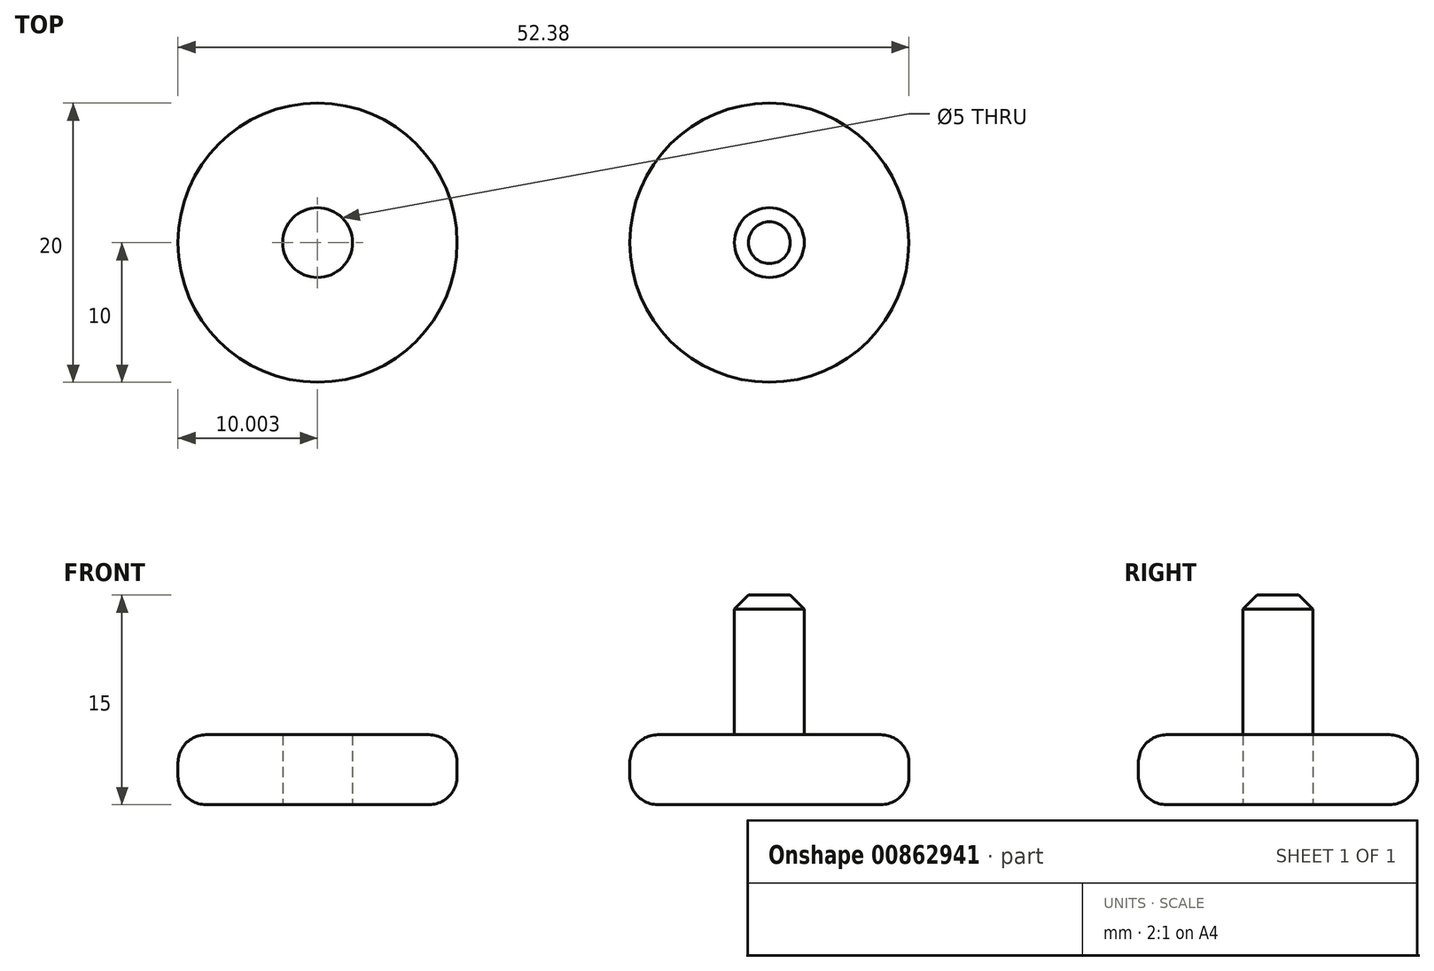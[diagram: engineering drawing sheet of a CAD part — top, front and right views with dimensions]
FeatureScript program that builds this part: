
annotation { "Feature Type Name" : "Feature", "Feature Type Description" : "" }
export const myFeature = defineFeature(function(context is Context, id is Id, definition is map)
    precondition{}
    {
        {
            var Q0;
            Q0=qCreatedBy(makeId("Top.planeOp"),FACE);
            var sketch = newSketch(context, id + "F0", { "sketchPlane" : qUnion([Q0])});
            skCircle(sketch, "E0", {"center": v(0, 0) * mm, "radius": 10 * mm});
            skCircle(sketch, "E1", {"center": v(-32.38, 0) * mm, "radius": 10 * mm});
            skCircle(sketch, "E2", {"center": v(-32.38, 0) * mm, "radius": 2.5 * mm});
            skSolve(sketch);
        }
        {
            var Q0;
            Q0=makeQuery(id+"F0.imprint","IMPRINT",FACE,{"disambiguationData":[TD([[makeQuery(id+"F0.imprint","IMPRINT",EDGE,{"derivedFrom":sQuery(id+"F0.wireOp",EDGE,"E0")}),1.0]])]});
            extrude(context, id + "F1", {"entities" : qUnion([Q0]), "depth" : 5 * mm, "offsetDistance" : 25 * mm});
        }
        {
            var Q0;
            Q0=makeQuery(id+"F1.opExtrude","CAP_FACE",FACE,{"disambiguationData":[OSD([sQuery(id+"F0.wireOp",EDGE,"E0")])],"isStart":false});
            var sketch = newSketch(context, id + "F2", { "sketchPlane" : qUnion([Q0])});
            skCircle(sketch, "E3", {"center": v(0, 0) * mm, "radius": 2.5 * mm});
            skSolve(sketch);
        }
        {
            var Q0;
            Q0=makeQuery(id+"F2.imprint","IMPRINT",FACE,{"disambiguationData":[TD([[makeQuery(id+"F2.imprint","IMPRINT",EDGE,{"derivedFrom":sQuery(id+"F2.wireOp",EDGE,"E3")}),1.0]])]});
            extrude(context, id + "F3", {"entities" : qUnion([Q0]), "operationType" : NewBodyOperationType.ADD, "depth" : 10 * mm, "offsetDistance" : 25 * mm});
        }
        {
            var Q0;
            Q0=makeQuery(id+"F3.opExtrude","CAP_EDGE",EDGE,{"disambiguationData":[OSD([sQuery(id+"F2.wireOp",EDGE,"E3")])],"isStart":false});
            chamfer(context, id + "F4", {"entities" : qUnion([Q0]), "width" : 1 * mm, "tangentPropagation" : true});
        }
        {
            var Q0;
            Q0=makeQuery(id+"F1.opExtrude","CAP_EDGE",EDGE,{"disambiguationData":[OSD([sQuery(id+"F0.wireOp",EDGE,"E0")])],"isStart":false});
            var Q1;
            Q1=makeQuery(id+"F1.opExtrude","CAP_EDGE",EDGE,{"disambiguationData":[OSD([sQuery(id+"F0.wireOp",EDGE,"E0")])],"isStart":true});
            fillet(context, id + "F5", {"entities" : qUnion([Q0, Q1]), "radius" : 2 * mm, "tangentPropagation" : true, "allowEdgeOverflow" : false});
        }
        {
            var Q0;
            Q0 = qSketchRegion(id + "F0", true);
            extrude(context, id + "F6", {"entities" : qUnion([Q0]), "operationType" : NewBodyOperationType.ADD, "depth" : 5 * mm, "offsetDistance" : 25 * mm});
        }
        {
            var Q0;
            Q0=makeQuery(id+"F6.opExtrude","CAP_EDGE",EDGE,{"disambiguationData":[OSD([sQuery(id+"F0.wireOp",EDGE,"E1")])],"isStart":false});
            var Q1;
            Q1=makeQuery(id+"F6.opExtrude","CAP_EDGE",EDGE,{"disambiguationData":[OSD([sQuery(id+"F0.wireOp",EDGE,"E1")])],"isStart":true});
            var Q2;
            Q2=makeQuery(id+"F6.opExtrude","CAP_EDGE",EDGE,{"disambiguationData":[OSD([sQuery(id+"F0.wireOp",EDGE,"E0")])],"isStart":false});
            var Q3;
            Q3=makeQuery(id+"F6.opExtrude","CAP_EDGE",EDGE,{"disambiguationData":[OSD([sQuery(id+"F0.wireOp",EDGE,"E0")])],"isStart":true});
            fillet(context, id + "F7", {"entities" : qUnion([Q0, Q1, Q2, Q3]), "radius" : 2 * mm, "tangentPropagation" : true, "allowEdgeOverflow" : false});
        }
    });
